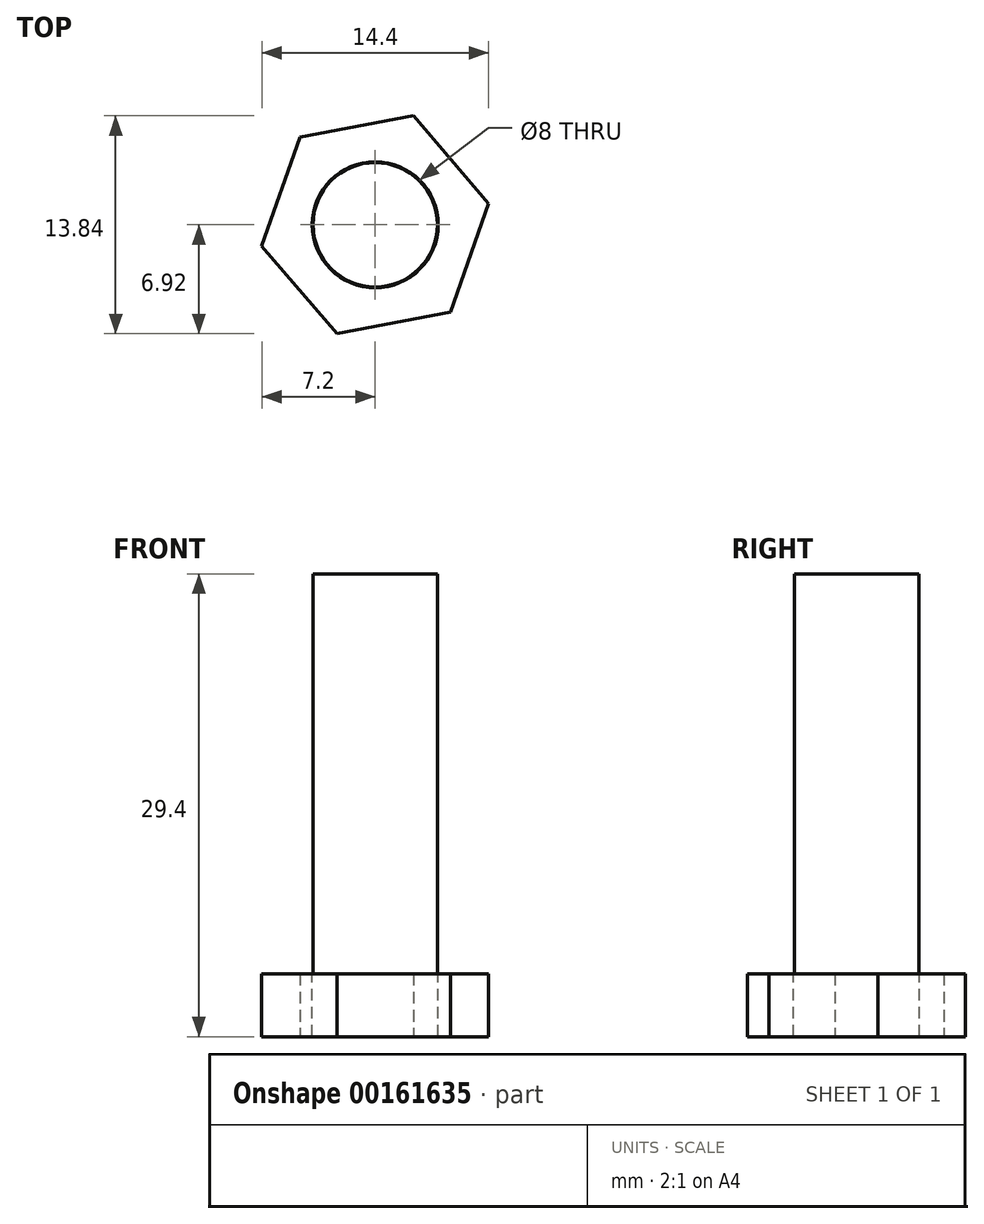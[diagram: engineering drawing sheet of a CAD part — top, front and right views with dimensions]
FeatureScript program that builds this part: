
annotation { "Feature Type Name" : "Feature", "Feature Type Description" : "" }
export const myFeature = defineFeature(function(context is Context, id is Id, definition is map)
    precondition{}
    {
        {
            var Q0;
            Q0=qCreatedBy(makeId("Top.planeOp"),FACE);
            var sketch = newSketch(context, id + "F0", { "sketchPlane" : qUnion([Q0])});
            skCircle(sketch, "E0.cCircle", {"center": v(0, 0) * mm, "radius": 6.35 * mm, "construction": true});
            skLineSegment(sketch, "E0.0", {"start": v(-4.78, 5.56) * mm, "end": v(2.43, 6.92) * mm});
            skLineSegment(sketch, "E0.1", {"start": v(2.43, 6.92) * mm, "end": v(7.2, 1.36) * mm});
            skLineSegment(sketch, "E0.2", {"start": v(7.2, 1.36) * mm, "end": v(4.78, -5.56) * mm});
            skLineSegment(sketch, "E0.3", {"start": v(4.78, -5.56) * mm, "end": v(-2.43, -6.92) * mm});
            skLineSegment(sketch, "E0.4", {"start": v(-2.43, -6.92) * mm, "end": v(-7.2, -1.36) * mm});
            skLineSegment(sketch, "E0.5", {"start": v(-7.2, -1.36) * mm, "end": v(-4.78, 5.56) * mm});
            skPoint(sketch, "E0.0.midPoint", {"position": v(-1.18, 6.24) * mm});
            skSolve(sketch);
        }
        {
            var Q0;
            Q0 = qSketchRegion(id + "F0", true);
            extrude(context, id + "F1", {"entities" : qUnion([Q0]), "endBound" : BoundingType.SYMMETRIC, "depth" : 4 * mm});
        }
        {
            var Q0;
            Q0=makeQuery(id+"F1.opExtrude","CAP_FACE",FACE,{"disambiguationData":[OSD([sQuery(id+"F0.wireOp",EDGE,"E0.0"),sQuery(id+"F0.wireOp",EDGE,"E0.1"),sQuery(id+"F0.wireOp",EDGE,"E0.2"),sQuery(id+"F0.wireOp",EDGE,"E0.3"),sQuery(id+"F0.wireOp",EDGE,"E0.4"),sQuery(id+"F0.wireOp",EDGE,"E0.5")])],"isStart":false});
            var sketch = newSketch(context, id + "F2", { "sketchPlane" : qUnion([Q0])});
            skCircle(sketch, "E1", {"center": v(0, 0) * mm, "radius": 4 * mm});
            skSolve(sketch);
        }
        {
            var Q0;
            Q0=makeQuery(id+"F2.imprint","IMPRINT",FACE,{"disambiguationData":[TD([[makeQuery(id+"F2.imprint","IMPRINT",EDGE,{"derivedFrom":sQuery(id+"F2.wireOp",EDGE,"E1")}),1.0]])]});
            extrude(context, id + "F3", {"entities" : qUnion([Q0]), "operationType" : NewBodyOperationType.REMOVE, "oppositeDirection" : true, "depth" : 25 * mm});
        }
        {
            var Q0;
            Q0=makeQuery(id+"F1.opExtrude","CAP_FACE",FACE,{"disambiguationData":[OSD([sQuery(id+"F0.wireOp",EDGE,"E0.0"),sQuery(id+"F0.wireOp",EDGE,"E0.1"),sQuery(id+"F0.wireOp",EDGE,"E0.2"),sQuery(id+"F0.wireOp",EDGE,"E0.3"),sQuery(id+"F0.wireOp",EDGE,"E0.4"),sQuery(id+"F0.wireOp",EDGE,"E0.5")])],"isStart":false});
            var sketch = newSketch(context, id + "F4", { "sketchPlane" : qUnion([Q0])});
            skCircle(sketch, "E2", {"center": v(0, 0) * mm, "radius": 3.95 * mm});
            skSolve(sketch);
        }
        {
            var Q0;
            Q0 = qSketchRegion(id + "F4", true);
            extrude(context, id + "F5", {"entities" : qUnion([Q0]), "operationType" : NewBodyOperationType.ADD, "depth" : 25.4 * mm});
        }
    });
